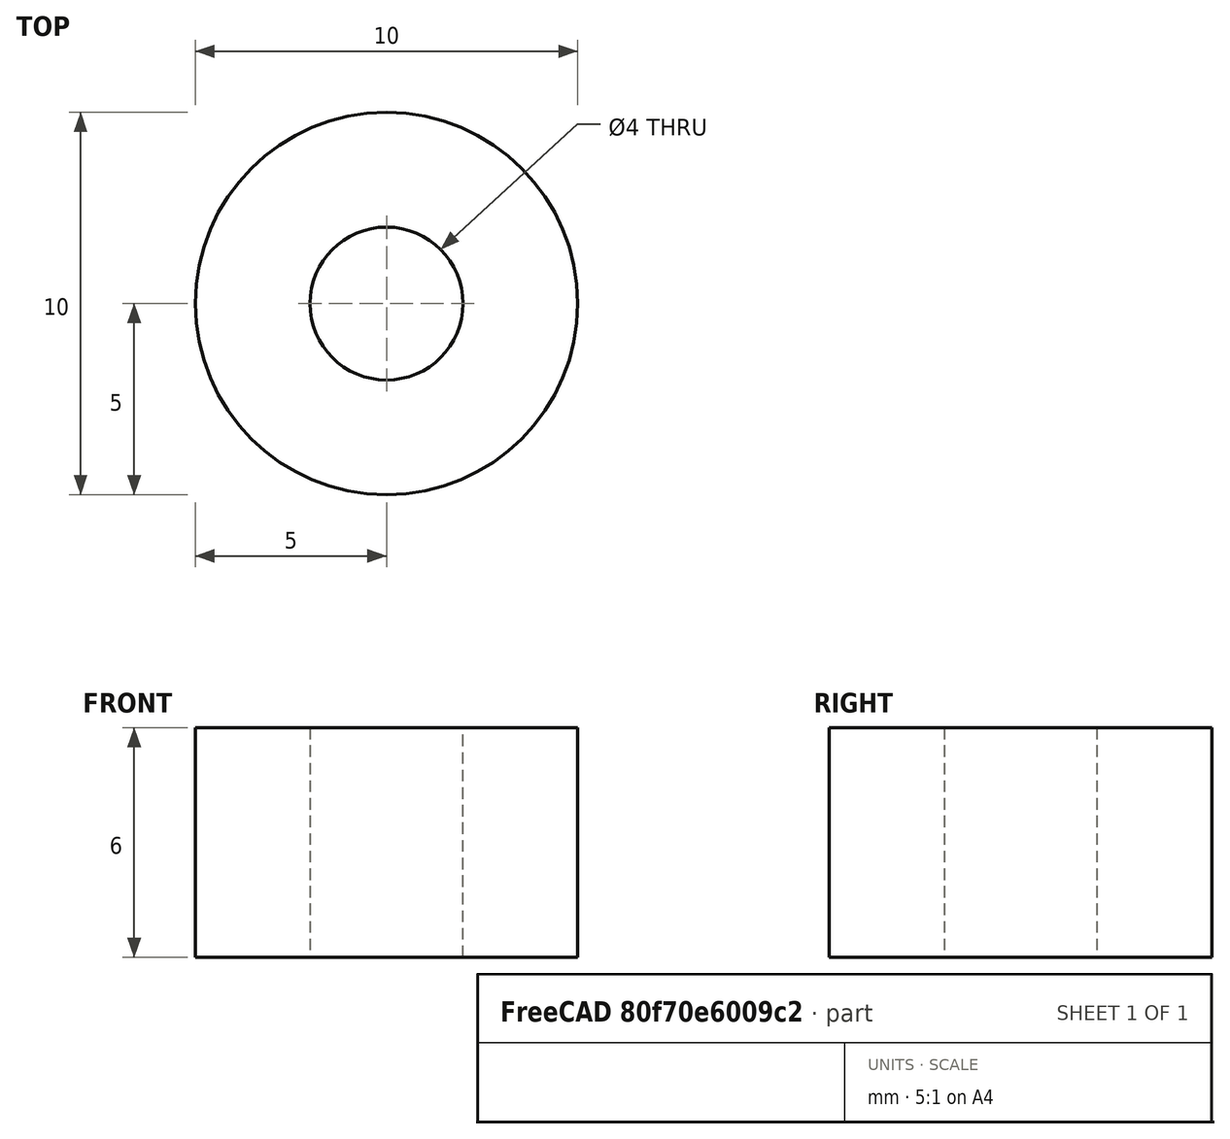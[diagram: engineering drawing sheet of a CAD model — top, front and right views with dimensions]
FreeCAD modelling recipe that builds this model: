
FCSTD DOCUMENT  (FreeCAD 0.20R29603 (Git))
Label: entretoise-cartes-vc-perc
License: Public Domain
LicenseURL: http://en.wikipedia.org/wiki/Public_domain
objects: Sketcher::SketchObject×1, PartDesign::Pad×1, PartDesign::Body×1
note: 4 computed .brp shape members not serialized (recipe doc carries the construction recipe); baked Part::Feature solids carry a one-line shape summary decoded from their .brp

FEATURE [Sketcher::SketchObject] Sketch
  FullyConstrained = true
  MapMode = 5
  Support = -> [XY_Plane]
  sketch-geometry (2):
    g0: Circle CenterX=0 CenterY=0 CenterZ=0 NormalX=0 NormalY=0 NormalZ=1 AngleXU=0 Radius=2
    g1: Circle CenterX=0 CenterY=0 CenterZ=0 NormalX=0 NormalY=0 NormalZ=1 AngleXU=0 Radius=5
  constraints (4):
    c: Coincident(g0,g-1)
    c: Diameter(g0) = 4
    c: Diameter(g1) = 10
    c: Coincident(g0,g1)
FEATURE [PartDesign::Pad] Pad
  Direction = (0,0,1)
  Length = 6
  Length2 = 10
  Profile = -> Sketch
  ReferenceAxis = -> Sketch [N_Axis]
  Type = 0
FEATURE [PartDesign::Body] Body
  Group = -> [Sketch,Pad]
  Origin = -> Origin
  Tip = -> Pad
